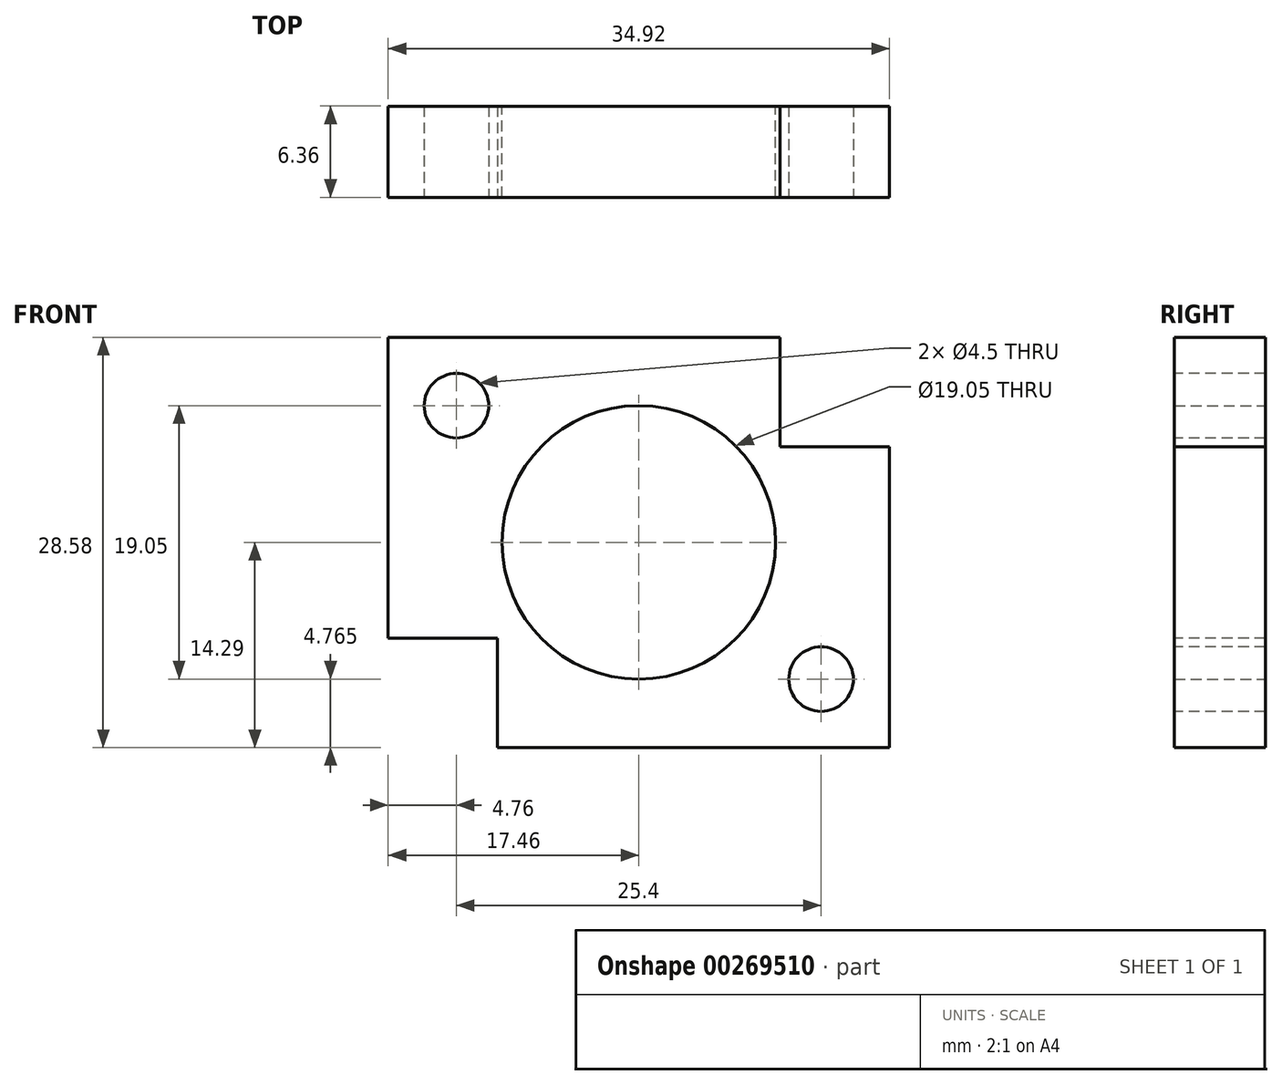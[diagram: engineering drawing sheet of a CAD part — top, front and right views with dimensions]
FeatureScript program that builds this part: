
annotation { "Feature Type Name" : "Feature", "Feature Type Description" : "" }
export const myFeature = defineFeature(function(context is Context, id is Id, definition is map)
    precondition{}
    {
        {
            var Q0;
            Q0=qCreatedBy(makeId("Front.planeOp"),FACE);
            var sketch = newSketch(context, id + "F0", { "sketchPlane" : qUnion([Q0])});
            skLineSegment(sketch, "E0.bottom", {"start": v(17.46, 14.29) * mm, "end": v(-17.46, 14.29) * mm});
            skLineSegment(sketch, "E0.top", {"start": v(17.46, -14.29) * mm, "end": v(-17.46, -14.29) * mm});
            skLineSegment(sketch, "E0.left", {"start": v(17.46, 14.29) * mm, "end": v(17.46, -14.29) * mm});
            skLineSegment(sketch, "E0.right", {"start": v(-17.46, 14.29) * mm, "end": v(-17.46, -14.29) * mm});
            skPoint(sketch, "E0.middle", {"position": v(0, 0) * mm});
            skCircle(sketch, "E1", {"center": v(0, 0) * mm, "radius": 9.53 * mm});
            skSolve(sketch);
        }
        {
            var Q0;
            Q0 = qSketchRegion(id + "F0", true);
            extrude(context, id + "F1", {"entities" : qUnion([Q0]), "endBound" : BoundingType.SYMMETRIC, "depth" : 6.35 * mm});
        }
        {
            var Q0;
            Q0=makeQuery(id+"F1.opExtrude","CAP_FACE",FACE,{"disambiguationData":[OSD([sQuery(id+"F0.wireOp",EDGE,"E0.bottom"),sQuery(id+"F0.wireOp",EDGE,"E0.top"),sQuery(id+"F0.wireOp",EDGE,"E0.left"),sQuery(id+"F0.wireOp",EDGE,"E0.right"),sQuery(id+"F0.wireOp",EDGE,"E1")])],"isStart":false});
            var sketch = newSketch(context, id + "F2", { "sketchPlane" : qUnion([Q0])});
            skLineSegment(sketch, "E2.bottom", {"start": v(12.7, 9.52) * mm, "end": v(-12.7, 9.52) * mm});
            skLineSegment(sketch, "E2.top", {"start": v(12.7, -9.53) * mm, "end": v(-12.7, -9.53) * mm});
            skLineSegment(sketch, "E2.left", {"start": v(12.7, 9.52) * mm, "end": v(12.7, -9.53) * mm});
            skLineSegment(sketch, "E2.right", {"start": v(-12.7, 9.52) * mm, "end": v(-12.7, -9.53) * mm});
            skPoint(sketch, "E2.middle", {"position": v(0, 0) * mm});
            skSolve(sketch);
        }
        {
            var Q0;
            Q0=sQuery(id+"F2.wireOp",VERTEX,"E2.right.start");
            var Q1;
            Q1=sQuery(id+"F2.wireOp",VERTEX,"E2.left.end");
            var Q2;
            Q2=makeQuery(id+"F1.opExtrude","SWEPT_BODY",BODY,{"disambiguationData":[OSD([sQuery(id+"F0.wireOp",EDGE,"E0.bottom"),sQuery(id+"F0.wireOp",EDGE,"E0.top"),sQuery(id+"F0.wireOp",EDGE,"E0.left"),sQuery(id+"F0.wireOp",EDGE,"E0.right"),sQuery(id+"F0.wireOp",EDGE,"E1")])]});
            hole(context, id + "F3", {"style" : HoleStyle.SIMPLE, "endStyle" : HoleEndStyle.THROUGH, "standardTappedOrClearance" : lookupTablePath({ "standard" : "ANSI", "fit" : "Normal (ASME)", "size" : "#8", "type" : "Clearance" }), "standardBlindInLast" : lookupTablePath({ "fit" : "Free", "standard" : "ANSI", "size" : "#8", "type" : "Clearance" }), "holeDiameter" : 4.5 * mm, "tappedDepth" : 10.16 * mm, "tapClearance" : 3, "locations" : qUnion([Q0, Q1]), "scope" : qUnion([Q2])});
        }
        {
            var Q0;
            Q0=makeQuery(id+"F1.opExtrude","CAP_FACE",FACE,{"disambiguationData":[OSD([sQuery(id+"F0.wireOp",EDGE,"E0.bottom"),sQuery(id+"F0.wireOp",EDGE,"E0.top"),sQuery(id+"F0.wireOp",EDGE,"E0.left"),sQuery(id+"F0.wireOp",EDGE,"E0.right"),sQuery(id+"F0.wireOp",EDGE,"E1")])],"isStart":false});
            var sketch = newSketch(context, id + "F4", { "sketchPlane" : qUnion([Q0])});
            skLineSegment(sketch, "E3.bottom", {"start": v(17.46, 14.29) * mm, "end": v(9.84, 14.29) * mm});
            skLineSegment(sketch, "E3.top", {"start": v(17.46, 6.67) * mm, "end": v(9.84, 6.67) * mm});
            skLineSegment(sketch, "E3.left", {"start": v(17.46, 14.29) * mm, "end": v(17.46, 6.67) * mm});
            skLineSegment(sketch, "E3.right", {"start": v(9.84, 14.29) * mm, "end": v(9.84, 6.67) * mm});
            skLineSegment(sketch, "E4.bottom", {"start": v(-17.46, -14.29) * mm, "end": v(-9.84, -14.29) * mm});
            skLineSegment(sketch, "E4.top", {"start": v(-17.46, -6.67) * mm, "end": v(-9.84, -6.67) * mm});
            skLineSegment(sketch, "E4.left", {"start": v(-17.46, -14.29) * mm, "end": v(-17.46, -6.67) * mm});
            skLineSegment(sketch, "E4.right", {"start": v(-9.84, -14.29) * mm, "end": v(-9.84, -6.67) * mm});
            skSolve(sketch);
        }
        {
            var Q0;
            Q0=makeQuery(id+"F4.imprint","IMPRINT",FACE,{"disambiguationData":[TD([[makeQuery(id+"F4.imprint","IMPRINT",EDGE,{"derivedFrom":sQuery(id+"F4.wireOp",EDGE,"E4.bottom")}),-1.0]])]});
            var Q1;
            Q1=makeQuery(id+"F4.imprint","IMPRINT",FACE,{"disambiguationData":[TD([[makeQuery(id+"F4.imprint","IMPRINT",EDGE,{"derivedFrom":sQuery(id+"F4.wireOp",EDGE,"E3.bottom")}),1.0]])]});
            extrude(context, id + "F5", {"entities" : qUnion([Q0, Q1]), "operationType" : NewBodyOperationType.REMOVE, "endBound" : BoundingType.THROUGH_ALL, "oppositeDirection" : true, "depth" : 25.4 * mm});
        }
    });
